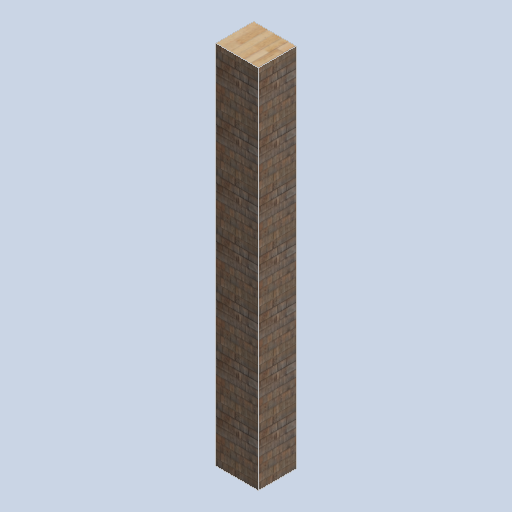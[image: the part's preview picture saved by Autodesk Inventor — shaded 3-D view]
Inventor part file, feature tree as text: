
AUTODESK INVENTOR PART (.ipt)
format: ipt  version: 2024.2 (Build 282272000, 272)  size: 165,376 bytes
history: native  units: in
note: dims shown in document units (in); Inventor stores cm internally (conversion verified against a paired STEP export)
features: other x3, sketch x1
ambient origin geometry x8: Origin, YZ Plane, XZ Plane, XY Plane, X Axis, Y Axis, Z Axis, Center Point
bodies: Solid1 (feature_tree)
feature tree (4):
  other  "support_column_01.ipt"
  other  "Solid1::support_column_01.ipt"
  other  "TaggingFeature1"
  sketch  "Sketch1"  dims[d0=0.3937in]
